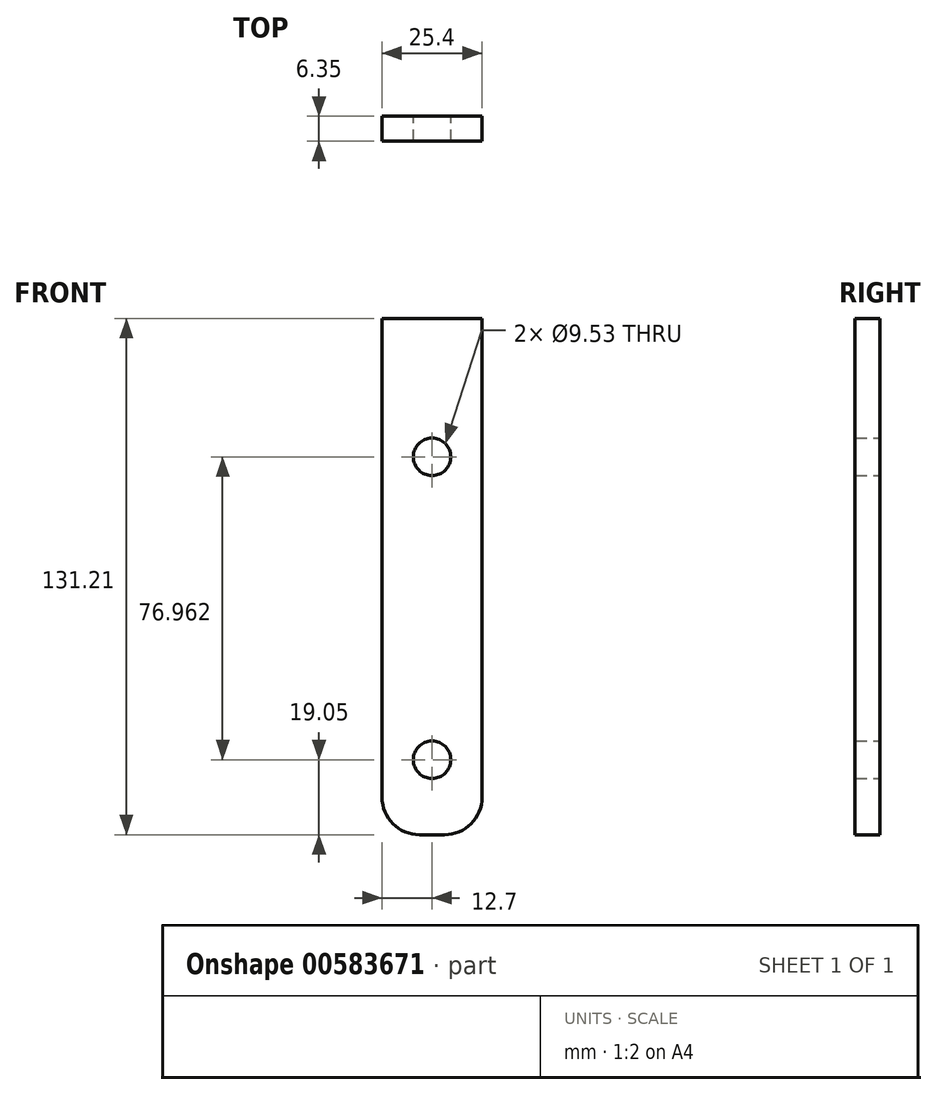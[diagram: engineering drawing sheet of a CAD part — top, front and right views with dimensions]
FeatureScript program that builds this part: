
annotation { "Feature Type Name" : "Feature", "Feature Type Description" : "" }
export const myFeature = defineFeature(function(context is Context, id is Id, definition is map)
    precondition{}
    {
        {
            var Q0;
            Q0=qCreatedBy(makeId("Front.planeOp"),FACE);
            var sketch = newSketch(context, id + "F0", { "sketchPlane" : qUnion([Q0])});
            skLineSegment(sketch, "E0", {"start": v(12.7, -9.52) * mm, "end": v(12.7, 112.16) * mm});
            skLineSegment(sketch, "E1", {"start": v(12.7, 112.16) * mm, "end": v(-12.7, 112.16) * mm});
            skLineSegment(sketch, "E2", {"start": v(-12.7, 112.16) * mm, "end": v(-12.7, -9.53) * mm});
            skLineSegment(sketch, "E3", {"start": v(3.18, -19.05) * mm, "end": v(-3.18, -19.05) * mm});
            skCircle(sketch, "E4", {"center": v(0, 0) * mm, "radius": 4.76 * mm});
            skCircle(sketch, "E5", {"center": v(0, 76.96) * mm, "radius": 4.76 * mm});
            skPoint(sketch, "E6.visualSharp", {"position": v(12.7, -19.05) * mm});
            skArc(sketch, "E6.filletArc", {"start": v(3.18, -19.05) * mm, "mid": v(9.91, -16.26) * mm, "end": v(12.7, -9.53) * mm});
            skPoint(sketch, "E7.visualSharp", {"position": v(-12.7, -19.05) * mm});
            skArc(sketch, "E7.filletArc", {"start": v(-12.7, -9.53) * mm, "mid": v(-9.91, -16.26) * mm, "end": v(-3.18, -19.05) * mm});
            skSolve(sketch);
        }
        {
            var Q0;
            Q0=makeQuery(id+"F0.imprint","IMPRINT",FACE,{"disambiguationData":[TD([[makeQuery(id+"F0.imprint","IMPRINT",EDGE,{"derivedFrom":sQuery(id+"F0.wireOp",EDGE,"E0")}),1.0]])]});
            extrude(context, id + "F1", {"entities" : qUnion([Q0]), "depth" : 6.35 * mm, "offsetDistance" : 25.4 * mm});
        }
    });
